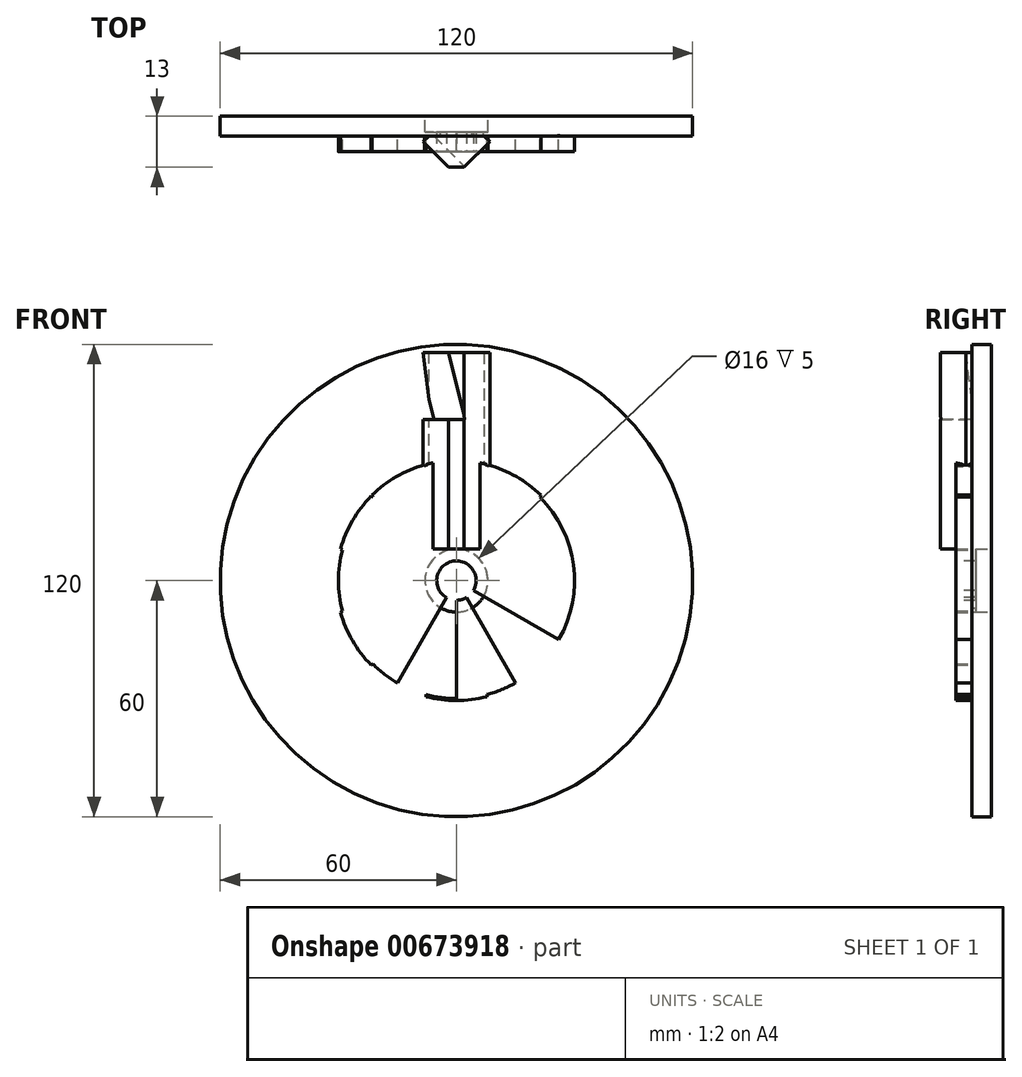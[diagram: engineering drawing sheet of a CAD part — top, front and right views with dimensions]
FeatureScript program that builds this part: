
annotation { "Feature Type Name" : "Feature", "Feature Type Description" : "" }
export const myFeature = defineFeature(function(context is Context, id is Id, definition is map)
    precondition{}
    {
        {
            var Q0;
            Q0=qCreatedBy(makeId("Front.planeOp"),FACE);
            var sketch = newSketch(context, id + "F0", { "sketchPlane" : qUnion([Q0])});
            skCircle(sketch, "E0", {"center": v(0, 0) * mm, "radius": 60 * mm});
            skCircle(sketch, "E1", {"center": v(0, 0) * mm, "radius": 30 * mm});
            skLineSegment(sketch, "E2", {"start": v(0, 60) * mm, "end": v(0, -60) * mm});
            skLineSegment(sketch, "E3", {"start": v(-60, 0) * mm, "end": v(60, 0) * mm});
            skLineSegment(sketch, "E4", {"start": v(0, 0) * mm, "end": v(51.96, -30) * mm});
            skLineSegment(sketch, "E5", {"start": v(51.96, -30) * mm, "end": v(-51.96, 30) * mm});
            skLineSegment(sketch, "E6", {"start": v(0, 0) * mm, "end": v(30, -51.96) * mm});
            skLineSegment(sketch, "E7", {"start": v(30, -51.96) * mm, "end": v(-30, 51.96) * mm});
            skLineSegment(sketch, "E8", {"start": v(0, 0) * mm, "end": v(-30, -51.96) * mm});
            skLineSegment(sketch, "E9", {"start": v(-30, -51.96) * mm, "end": v(30, 51.96) * mm});
            skLineSegment(sketch, "E10", {"start": v(0, 0) * mm, "end": v(51.96, 30) * mm});
            skLineSegment(sketch, "E11", {"start": v(51.96, 30) * mm, "end": v(-51.96, -30) * mm});
            skCircle(sketch, "E12", {"center": v(0, 0) * mm, "radius": 57.5 * mm});
            skLineSegment(sketch, "E13", {"start": v(0, 57.5) * mm, "end": v(-5, 57.28) * mm});
            skLineSegment(sketch, "E14", {"start": v(-28.75, 49.8) * mm, "end": v(-24.32, 52.1) * mm});
            skLineSegment(sketch, "E15", {"start": v(-24.32, 52.1) * mm, "end": v(-7.76, 28.98) * mm});
            skLineSegment(sketch, "E16", {"start": v(-7.76, 28.98) * mm, "end": v(-5, 57.28) * mm});
            skLineSegment(sketch, "E17.1.0", {"start": v(5, 57.28) * mm, "end": v(7.76, 28.98) * mm});
            skLineSegment(sketch, "E17.1.1", {"start": v(7.76, 28.98) * mm, "end": v(24.32, 52.1) * mm});
            skLineSegment(sketch, "E17.2.0", {"start": v(32.97, 47.11) * mm, "end": v(21.21, 21.21) * mm});
            skLineSegment(sketch, "E17.2.1", {"start": v(21.21, 21.21) * mm, "end": v(47.11, 32.97) * mm});
            skLineSegment(sketch, "E17.3.0", {"start": v(52.1, 24.32) * mm, "end": v(28.98, 7.76) * mm});
            skLineSegment(sketch, "E17.3.1", {"start": v(28.98, 7.76) * mm, "end": v(57.28, 5) * mm});
            skLineSegment(sketch, "E17.4.0", {"start": v(57.28, -5) * mm, "end": v(28.98, -7.76) * mm});
            skLineSegment(sketch, "E17.4.1", {"start": v(28.98, -7.76) * mm, "end": v(52.1, -24.32) * mm});
            skLineSegment(sketch, "E17.5.0", {"start": v(47.11, -32.97) * mm, "end": v(21.21, -21.21) * mm});
            skLineSegment(sketch, "E17.5.1", {"start": v(21.21, -21.21) * mm, "end": v(32.97, -47.11) * mm});
            skLineSegment(sketch, "E17.6.0", {"start": v(24.32, -52.1) * mm, "end": v(7.76, -28.98) * mm});
            skLineSegment(sketch, "E17.6.1", {"start": v(7.76, -28.98) * mm, "end": v(5, -57.28) * mm});
            skLineSegment(sketch, "E17.7.0", {"start": v(-5, -57.28) * mm, "end": v(-7.76, -28.98) * mm});
            skLineSegment(sketch, "E17.7.1", {"start": v(-7.76, -28.98) * mm, "end": v(-24.32, -52.1) * mm});
            skLineSegment(sketch, "E17.8.0", {"start": v(-32.97, -47.11) * mm, "end": v(-21.21, -21.21) * mm});
            skLineSegment(sketch, "E17.8.1", {"start": v(-21.21, -21.21) * mm, "end": v(-47.11, -32.97) * mm});
            skLineSegment(sketch, "E17.9.0", {"start": v(-52.1, -24.32) * mm, "end": v(-28.98, -7.76) * mm});
            skLineSegment(sketch, "E17.9.1", {"start": v(-28.98, -7.76) * mm, "end": v(-57.28, -5) * mm});
            skLineSegment(sketch, "E17.10.0", {"start": v(-57.28, 5) * mm, "end": v(-28.98, 7.76) * mm});
            skLineSegment(sketch, "E17.10.1", {"start": v(-28.98, 7.76) * mm, "end": v(-52.1, 24.32) * mm});
            skLineSegment(sketch, "E17.anchor1", {"start": v(0, 0) * mm, "end": v(-7.76, 28.98) * mm, "construction": true});
            skLineSegment(sketch, "E17.anchor2", {"start": v(0, 0) * mm, "end": v(-21.21, 21.21) * mm, "construction": true});
            skLineSegment(sketch, "E18.2.11.0", {"start": v(-47.11, 32.97) * mm, "end": v(-21.21, 21.21) * mm});
            skLineSegment(sketch, "E18.3.11.0", {"start": v(-21.21, 21.21) * mm, "end": v(-32.97, 47.11) * mm});
            skCircle(sketch, "E19", {"center": v(0, 0) * mm, "radius": 30.5 * mm});
            skSolve(sketch);
        }
        {
            var Q0;
            {var subQ1=sQuery(id+"F0.wireOp",EDGE,"E1");var subQ3=sQuery(id+"F0.wireOp",EDGE,"E2");var subQ4=makeQuery(id+"F0.imprint","INTERSECT",VERTEX,{"disambiguationData":[OD(0.0)],"derivedFrom":[subQ1,subQ3]});Q0=makeQuery(id+"F0.imprint","IMPRINT",FACE,{"disambiguationData":[TD([[makeQuery(id+"F0.imprint","IMPRINT",EDGE,{"disambiguationData":[TD([[subQ4,1.0]])],"derivedFrom":subQ3}),1.0]])]});}
            var Q1;
            {var subQ1=sQuery(id+"F0.wireOp",EDGE,"E1");var subQ3=sQuery(id+"F0.wireOp",EDGE,"E7");var subQ4=makeQuery(id+"F0.imprint","INTERSECT",VERTEX,{"disambiguationData":[OD(0.0)],"derivedFrom":[subQ1,subQ3]});Q1=makeQuery(id+"F0.imprint","IMPRINT",FACE,{"disambiguationData":[TD([[makeQuery(id+"F0.imprint","IMPRINT",EDGE,{"disambiguationData":[TD([[subQ4,-1.0]])],"derivedFrom":subQ3}),1.0]])]});}
            var Q2;
            {var subQ1=sQuery(id+"F0.wireOp",EDGE,"E1");var subQ3=sQuery(id+"F0.wireOp",EDGE,"E5");var subQ4=makeQuery(id+"F0.imprint","INTERSECT",VERTEX,{"disambiguationData":[OD(0.0)],"derivedFrom":[subQ1,subQ3]});Q2=makeQuery(id+"F0.imprint","IMPRINT",FACE,{"disambiguationData":[TD([[makeQuery(id+"F0.imprint","IMPRINT",EDGE,{"disambiguationData":[TD([[subQ4,-1.0]])],"derivedFrom":subQ3}),-1.0]])]});}
            var Q3;
            {var subQ1=sQuery(id+"F0.wireOp",EDGE,"E1");var subQ3=sQuery(id+"F0.wireOp",EDGE,"E5");var subQ4=makeQuery(id+"F0.imprint","INTERSECT",VERTEX,{"disambiguationData":[OD(0.0)],"derivedFrom":[subQ1,subQ3]});Q3=makeQuery(id+"F0.imprint","IMPRINT",FACE,{"disambiguationData":[TD([[makeQuery(id+"F0.imprint","IMPRINT",EDGE,{"disambiguationData":[TD([[subQ4,-1.0]])],"derivedFrom":subQ3}),1.0]])]});}
            var Q4;
            {var subQ1=sQuery(id+"F0.wireOp",EDGE,"E1");var subQ3=sQuery(id+"F0.wireOp",EDGE,"E3");var subQ4=makeQuery(id+"F0.imprint","INTERSECT",VERTEX,{"disambiguationData":[OD(1.0)],"derivedFrom":[subQ1,subQ3]});Q4=makeQuery(id+"F0.imprint","IMPRINT",FACE,{"disambiguationData":[TD([[makeQuery(id+"F0.imprint","IMPRINT",EDGE,{"disambiguationData":[TD([[subQ4,1.0]])],"derivedFrom":subQ3}),1.0]])]});}
            var Q5;
            {var subQ1=sQuery(id+"F0.wireOp",EDGE,"E1");var subQ3=sQuery(id+"F0.wireOp",EDGE,"E3");var subQ4=makeQuery(id+"F0.imprint","INTERSECT",VERTEX,{"disambiguationData":[OD(1.0)],"derivedFrom":[subQ1,subQ3]});Q5=makeQuery(id+"F0.imprint","IMPRINT",FACE,{"disambiguationData":[TD([[makeQuery(id+"F0.imprint","IMPRINT",EDGE,{"disambiguationData":[TD([[subQ4,1.0]])],"derivedFrom":subQ3}),-1.0]])]});}
            var Q6;
            {var subQ1=sQuery(id+"F0.wireOp",EDGE,"E1");var subQ3=sQuery(id+"F0.wireOp",EDGE,"E11");var subQ4=makeQuery(id+"F0.imprint","INTERSECT",VERTEX,{"disambiguationData":[OD(1.0)],"derivedFrom":[subQ1,subQ3]});Q6=makeQuery(id+"F0.imprint","IMPRINT",FACE,{"disambiguationData":[TD([[makeQuery(id+"F0.imprint","IMPRINT",EDGE,{"disambiguationData":[TD([[subQ4,-1.0]])],"derivedFrom":subQ3}),-1.0]])]});}
            var Q7;
            {var subQ1=sQuery(id+"F0.wireOp",EDGE,"E1");var subQ3=sQuery(id+"F0.wireOp",EDGE,"E11");var subQ4=makeQuery(id+"F0.imprint","INTERSECT",VERTEX,{"disambiguationData":[OD(1.0)],"derivedFrom":[subQ1,subQ3]});Q7=makeQuery(id+"F0.imprint","IMPRINT",FACE,{"disambiguationData":[TD([[makeQuery(id+"F0.imprint","IMPRINT",EDGE,{"disambiguationData":[TD([[subQ4,-1.0]])],"derivedFrom":subQ3}),1.0]])]});}
            var Q8;
            {var subQ1=sQuery(id+"F0.wireOp",EDGE,"E1");var subQ3=sQuery(id+"F0.wireOp",EDGE,"E9");var subQ4=makeQuery(id+"F0.imprint","INTERSECT",VERTEX,{"disambiguationData":[OD(1.0)],"derivedFrom":[subQ1,subQ3]});Q8=makeQuery(id+"F0.imprint","IMPRINT",FACE,{"disambiguationData":[TD([[makeQuery(id+"F0.imprint","IMPRINT",EDGE,{"disambiguationData":[TD([[subQ4,1.0]])],"derivedFrom":subQ3}),1.0]])]});}
            var Q9;
            {var subQ1=sQuery(id+"F0.wireOp",EDGE,"E1");var subQ3=sQuery(id+"F0.wireOp",EDGE,"E9");var subQ4=makeQuery(id+"F0.imprint","INTERSECT",VERTEX,{"disambiguationData":[OD(1.0)],"derivedFrom":[subQ1,subQ3]});Q9=makeQuery(id+"F0.imprint","IMPRINT",FACE,{"disambiguationData":[TD([[makeQuery(id+"F0.imprint","IMPRINT",EDGE,{"disambiguationData":[TD([[subQ4,1.0]])],"derivedFrom":subQ3}),-1.0]])]});}
            var Q10;
            {var subQ1=sQuery(id+"F0.wireOp",EDGE,"E1");var subQ3=sQuery(id+"F0.wireOp",EDGE,"E2");var subQ4=makeQuery(id+"F0.imprint","INTERSECT",VERTEX,{"disambiguationData":[OD(1.0)],"derivedFrom":[subQ1,subQ3]});Q10=makeQuery(id+"F0.imprint","IMPRINT",FACE,{"disambiguationData":[TD([[makeQuery(id+"F0.imprint","IMPRINT",EDGE,{"disambiguationData":[TD([[subQ4,-1.0]])],"derivedFrom":subQ3}),-1.0]])]});}
            var Q11;
            {var subQ1=sQuery(id+"F0.wireOp",EDGE,"E1");var subQ3=sQuery(id+"F0.wireOp",EDGE,"E2");var subQ4=makeQuery(id+"F0.imprint","INTERSECT",VERTEX,{"disambiguationData":[OD(1.0)],"derivedFrom":[subQ1,subQ3]});Q11=makeQuery(id+"F0.imprint","IMPRINT",FACE,{"disambiguationData":[TD([[makeQuery(id+"F0.imprint","IMPRINT",EDGE,{"disambiguationData":[TD([[subQ4,-1.0]])],"derivedFrom":subQ3}),1.0]])]});}
            var Q12;
            {var subQ1=sQuery(id+"F0.wireOp",EDGE,"E1");var subQ3=sQuery(id+"F0.wireOp",EDGE,"E7");var subQ4=makeQuery(id+"F0.imprint","INTERSECT",VERTEX,{"disambiguationData":[OD(1.0)],"derivedFrom":[subQ1,subQ3]});Q12=makeQuery(id+"F0.imprint","IMPRINT",FACE,{"disambiguationData":[TD([[makeQuery(id+"F0.imprint","IMPRINT",EDGE,{"disambiguationData":[TD([[subQ4,1.0]])],"derivedFrom":subQ3}),1.0]])]});}
            var Q13;
            {var subQ1=sQuery(id+"F0.wireOp",EDGE,"E1");var subQ3=sQuery(id+"F0.wireOp",EDGE,"E5");var subQ4=makeQuery(id+"F0.imprint","INTERSECT",VERTEX,{"disambiguationData":[OD(1.0)],"derivedFrom":[subQ1,subQ3]});Q13=makeQuery(id+"F0.imprint","IMPRINT",FACE,{"disambiguationData":[TD([[makeQuery(id+"F0.imprint","IMPRINT",EDGE,{"disambiguationData":[TD([[subQ4,1.0]])],"derivedFrom":subQ3}),1.0]])]});}
            var Q14;
            {var subQ1=sQuery(id+"F0.wireOp",EDGE,"E1");var subQ3=sQuery(id+"F0.wireOp",EDGE,"E5");var subQ4=makeQuery(id+"F0.imprint","INTERSECT",VERTEX,{"disambiguationData":[OD(1.0)],"derivedFrom":[subQ1,subQ3]});Q14=makeQuery(id+"F0.imprint","IMPRINT",FACE,{"disambiguationData":[TD([[makeQuery(id+"F0.imprint","IMPRINT",EDGE,{"disambiguationData":[TD([[subQ4,1.0]])],"derivedFrom":subQ3}),-1.0]])]});}
            var Q15;
            {var subQ1=sQuery(id+"F0.wireOp",EDGE,"E1");var subQ3=sQuery(id+"F0.wireOp",EDGE,"E3");var subQ4=makeQuery(id+"F0.imprint","INTERSECT",VERTEX,{"disambiguationData":[OD(0.0)],"derivedFrom":[subQ1,subQ3]});Q15=makeQuery(id+"F0.imprint","IMPRINT",FACE,{"disambiguationData":[TD([[makeQuery(id+"F0.imprint","IMPRINT",EDGE,{"disambiguationData":[TD([[subQ4,-1.0]])],"derivedFrom":subQ3}),-1.0]])]});}
            var Q16;
            {var subQ1=sQuery(id+"F0.wireOp",EDGE,"E1");var subQ3=sQuery(id+"F0.wireOp",EDGE,"E3");var subQ4=makeQuery(id+"F0.imprint","INTERSECT",VERTEX,{"disambiguationData":[OD(0.0)],"derivedFrom":[subQ1,subQ3]});Q16=makeQuery(id+"F0.imprint","IMPRINT",FACE,{"disambiguationData":[TD([[makeQuery(id+"F0.imprint","IMPRINT",EDGE,{"disambiguationData":[TD([[subQ4,-1.0]])],"derivedFrom":subQ3}),1.0]])]});}
            var Q17;
            {var subQ1=sQuery(id+"F0.wireOp",EDGE,"E1");var subQ3=sQuery(id+"F0.wireOp",EDGE,"E11");var subQ4=makeQuery(id+"F0.imprint","INTERSECT",VERTEX,{"disambiguationData":[OD(0.0)],"derivedFrom":[subQ1,subQ3]});Q17=makeQuery(id+"F0.imprint","IMPRINT",FACE,{"disambiguationData":[TD([[makeQuery(id+"F0.imprint","IMPRINT",EDGE,{"disambiguationData":[TD([[subQ4,1.0]])],"derivedFrom":subQ3}),1.0]])]});}
            var Q18;
            {var subQ1=sQuery(id+"F0.wireOp",EDGE,"E1");var subQ3=sQuery(id+"F0.wireOp",EDGE,"E11");var subQ4=makeQuery(id+"F0.imprint","INTERSECT",VERTEX,{"disambiguationData":[OD(0.0)],"derivedFrom":[subQ1,subQ3]});Q18=makeQuery(id+"F0.imprint","IMPRINT",FACE,{"disambiguationData":[TD([[makeQuery(id+"F0.imprint","IMPRINT",EDGE,{"disambiguationData":[TD([[subQ4,1.0]])],"derivedFrom":subQ3}),-1.0]])]});}
            var Q19;
            {var subQ1=sQuery(id+"F0.wireOp",EDGE,"E1");var subQ3=sQuery(id+"F0.wireOp",EDGE,"E9");var subQ4=makeQuery(id+"F0.imprint","INTERSECT",VERTEX,{"disambiguationData":[OD(0.0)],"derivedFrom":[subQ1,subQ3]});Q19=makeQuery(id+"F0.imprint","IMPRINT",FACE,{"disambiguationData":[TD([[makeQuery(id+"F0.imprint","IMPRINT",EDGE,{"disambiguationData":[TD([[subQ4,-1.0]])],"derivedFrom":subQ3}),-1.0]])]});}
            var Q20;
            {var subQ1=sQuery(id+"F0.wireOp",EDGE,"E1");var subQ3=sQuery(id+"F0.wireOp",EDGE,"E9");var subQ4=makeQuery(id+"F0.imprint","INTERSECT",VERTEX,{"disambiguationData":[OD(0.0)],"derivedFrom":[subQ1,subQ3]});Q20=makeQuery(id+"F0.imprint","IMPRINT",FACE,{"disambiguationData":[TD([[makeQuery(id+"F0.imprint","IMPRINT",EDGE,{"disambiguationData":[TD([[subQ4,-1.0]])],"derivedFrom":subQ3}),1.0]])]});}
            var Q21;
            {var subQ1=sQuery(id+"F0.wireOp",EDGE,"E1");var subQ3=sQuery(id+"F0.wireOp",EDGE,"E7");var subQ4=makeQuery(id+"F0.imprint","INTERSECT",VERTEX,{"disambiguationData":[OD(1.0)],"derivedFrom":[subQ1,subQ3]});Q21=makeQuery(id+"F0.imprint","IMPRINT",FACE,{"disambiguationData":[TD([[makeQuery(id+"F0.imprint","IMPRINT",EDGE,{"disambiguationData":[TD([[subQ4,1.0]])],"derivedFrom":subQ3}),-1.0]])]});}
            var Q22;
            {var subQ0=sQuery(id+"F0.wireOp",EDGE,"E1");var subQ2=sQuery(id+"F0.wireOp",EDGE,"E7");var subQ3=makeQuery(id+"F0.imprint","INTERSECT",VERTEX,{"disambiguationData":[OD(1.0)],"derivedFrom":[subQ0,subQ2]});Q22=makeQuery(id+"F0.imprint","IMPRINT",FACE,{"disambiguationData":[TD([[makeQuery(id+"F0.imprint","IMPRINT",EDGE,{"disambiguationData":[TD([[subQ3,-1.0]])],"derivedFrom":subQ0}),1.0]])]});}
            var Q23;
            {var subQ0=sQuery(id+"F0.wireOp",EDGE,"E1");var subQ2=sQuery(id+"F0.wireOp",EDGE,"E5");var subQ3=makeQuery(id+"F0.imprint","INTERSECT",VERTEX,{"disambiguationData":[OD(1.0)],"derivedFrom":[subQ0,subQ2]});Q23=makeQuery(id+"F0.imprint","IMPRINT",FACE,{"disambiguationData":[TD([[makeQuery(id+"F0.imprint","IMPRINT",EDGE,{"disambiguationData":[TD([[subQ3,-1.0]])],"derivedFrom":subQ0}),1.0]])]});}
            var Q24;
            {var subQ0=sQuery(id+"F0.wireOp",EDGE,"E1");var subQ2=sQuery(id+"F0.wireOp",EDGE,"E3");var subQ3=makeQuery(id+"F0.imprint","INTERSECT",VERTEX,{"disambiguationData":[OD(0.0)],"derivedFrom":[subQ0,subQ2]});Q24=makeQuery(id+"F0.imprint","IMPRINT",FACE,{"disambiguationData":[TD([[makeQuery(id+"F0.imprint","IMPRINT",EDGE,{"disambiguationData":[TD([[subQ3,-1.0]])],"derivedFrom":subQ0}),1.0]])]});}
            var Q25;
            {var subQ0=sQuery(id+"F0.wireOp",EDGE,"E1");var subQ2=sQuery(id+"F0.wireOp",EDGE,"E9");var subQ3=makeQuery(id+"F0.imprint","INTERSECT",VERTEX,{"disambiguationData":[OD(0.0)],"derivedFrom":[subQ0,subQ2]});Q25=makeQuery(id+"F0.imprint","IMPRINT",FACE,{"disambiguationData":[TD([[makeQuery(id+"F0.imprint","IMPRINT",EDGE,{"disambiguationData":[TD([[subQ3,-1.0]])],"derivedFrom":subQ0}),1.0]])]});}
            var Q26;
            {var subQ0=sQuery(id+"F0.wireOp",EDGE,"E1");var subQ2=sQuery(id+"F0.wireOp",EDGE,"E2");var subQ3=makeQuery(id+"F0.imprint","INTERSECT",VERTEX,{"disambiguationData":[OD(0.0)],"derivedFrom":[subQ0,subQ2]});Q26=makeQuery(id+"F0.imprint","IMPRINT",FACE,{"disambiguationData":[TD([[makeQuery(id+"F0.imprint","IMPRINT",EDGE,{"disambiguationData":[TD([[subQ3,-1.0]])],"derivedFrom":subQ0}),1.0]])]});}
            var Q27;
            {var subQ0=sQuery(id+"F0.wireOp",EDGE,"E1");var subQ2=sQuery(id+"F0.wireOp",EDGE,"E7");var subQ3=makeQuery(id+"F0.imprint","INTERSECT",VERTEX,{"disambiguationData":[OD(0.0)],"derivedFrom":[subQ0,subQ2]});Q27=makeQuery(id+"F0.imprint","IMPRINT",FACE,{"disambiguationData":[TD([[makeQuery(id+"F0.imprint","IMPRINT",EDGE,{"disambiguationData":[TD([[subQ3,-1.0]])],"derivedFrom":subQ0}),1.0]])]});}
            var Q28;
            {var subQ0=sQuery(id+"F0.wireOp",EDGE,"E1");var subQ2=sQuery(id+"F0.wireOp",EDGE,"E11");var subQ3=makeQuery(id+"F0.imprint","INTERSECT",VERTEX,{"disambiguationData":[OD(0.0)],"derivedFrom":[subQ0,subQ2]});Q28=makeQuery(id+"F0.imprint","IMPRINT",FACE,{"disambiguationData":[TD([[makeQuery(id+"F0.imprint","IMPRINT",EDGE,{"disambiguationData":[TD([[subQ3,-1.0]])],"derivedFrom":subQ0}),1.0]])]});}
            var Q29;
            {var subQ0=sQuery(id+"F0.wireOp",EDGE,"E1");var subQ2=sQuery(id+"F0.wireOp",EDGE,"E3");var subQ3=makeQuery(id+"F0.imprint","INTERSECT",VERTEX,{"disambiguationData":[OD(1.0)],"derivedFrom":[subQ0,subQ2]});Q29=makeQuery(id+"F0.imprint","IMPRINT",FACE,{"disambiguationData":[TD([[makeQuery(id+"F0.imprint","IMPRINT",EDGE,{"disambiguationData":[TD([[subQ3,-1.0]])],"derivedFrom":subQ0}),1.0]])]});}
            var Q30;
            {var subQ0=sQuery(id+"F0.wireOp",EDGE,"E1");var subQ2=sQuery(id+"F0.wireOp",EDGE,"E5");var subQ3=makeQuery(id+"F0.imprint","INTERSECT",VERTEX,{"disambiguationData":[OD(0.0)],"derivedFrom":[subQ0,subQ2]});Q30=makeQuery(id+"F0.imprint","IMPRINT",FACE,{"disambiguationData":[TD([[makeQuery(id+"F0.imprint","IMPRINT",EDGE,{"disambiguationData":[TD([[subQ3,-1.0]])],"derivedFrom":subQ0}),1.0]])]});}
            var Q31;
            {var subQ0=sQuery(id+"F0.wireOp",EDGE,"E1");var subQ2=sQuery(id+"F0.wireOp",EDGE,"E11");var subQ3=makeQuery(id+"F0.imprint","INTERSECT",VERTEX,{"disambiguationData":[OD(1.0)],"derivedFrom":[subQ0,subQ2]});Q31=makeQuery(id+"F0.imprint","IMPRINT",FACE,{"disambiguationData":[TD([[makeQuery(id+"F0.imprint","IMPRINT",EDGE,{"disambiguationData":[TD([[subQ3,-1.0]])],"derivedFrom":subQ0}),1.0]])]});}
            var Q32;
            {var subQ0=sQuery(id+"F0.wireOp",EDGE,"E1");var subQ2=sQuery(id+"F0.wireOp",EDGE,"E9");var subQ3=makeQuery(id+"F0.imprint","INTERSECT",VERTEX,{"disambiguationData":[OD(1.0)],"derivedFrom":[subQ0,subQ2]});Q32=makeQuery(id+"F0.imprint","IMPRINT",FACE,{"disambiguationData":[TD([[makeQuery(id+"F0.imprint","IMPRINT",EDGE,{"disambiguationData":[TD([[subQ3,-1.0]])],"derivedFrom":subQ0}),1.0]])]});}
            var Q33;
            {var subQ0=sQuery(id+"F0.wireOp",EDGE,"E1");var subQ2=sQuery(id+"F0.wireOp",EDGE,"E2");var subQ3=makeQuery(id+"F0.imprint","INTERSECT",VERTEX,{"disambiguationData":[OD(1.0)],"derivedFrom":[subQ0,subQ2]});Q33=makeQuery(id+"F0.imprint","IMPRINT",FACE,{"disambiguationData":[TD([[makeQuery(id+"F0.imprint","IMPRINT",EDGE,{"disambiguationData":[TD([[subQ3,-1.0]])],"derivedFrom":subQ0}),1.0]])]});}
            var Q34;
            {var subQ1=sQuery(id+"F0.wireOp",EDGE,"E1");var subQ3=sQuery(id+"F0.wireOp",EDGE,"E7");var subQ4=makeQuery(id+"F0.imprint","INTERSECT",VERTEX,{"disambiguationData":[OD(0.0)],"derivedFrom":[subQ1,subQ3]});Q34=makeQuery(id+"F0.imprint","IMPRINT",FACE,{"disambiguationData":[TD([[makeQuery(id+"F0.imprint","IMPRINT",EDGE,{"disambiguationData":[TD([[subQ4,-1.0]])],"derivedFrom":subQ3}),-1.0]])]});}
            var Q35;
            {var subQ1=sQuery(id+"F0.wireOp",EDGE,"E1");var subQ3=sQuery(id+"F0.wireOp",EDGE,"E2");var subQ4=makeQuery(id+"F0.imprint","INTERSECT",VERTEX,{"disambiguationData":[OD(0.0)],"derivedFrom":[subQ1,subQ3]});Q35=makeQuery(id+"F0.imprint","IMPRINT",FACE,{"disambiguationData":[TD([[makeQuery(id+"F0.imprint","IMPRINT",EDGE,{"disambiguationData":[TD([[subQ4,1.0]])],"derivedFrom":subQ3}),-1.0]])]});}
            extrude(context, id + "F1", {"entities" : qUnion([Q0, Q1, Q2, Q3, Q4, Q5, Q6, Q7, Q8, Q9, Q10, Q11, Q12, Q13, Q14, Q15, Q16, Q17, Q18, Q19, Q20, Q21, Q22, Q23, Q24, Q25, Q26, Q27, Q28, Q29, Q30, Q31, Q32, Q33, Q34, Q35]), "endBound" : BoundingType.SYMMETRIC, "depth" : 5 * mm, "offsetDistance" : 25 * mm});
        }
        {
            var Q0;
            Q0=qCreatedBy(makeId("Top.planeOp"),FACE);
            var sketch = newSketch(context, id + "F2", { "sketchPlane" : qUnion([Q0])});
            skCircle(sketch, "E20", {"center": v(0, 0) * mm, "radius": 25 * mm});
            skLineSegment(sketch, "E21", {"start": v(0, 0) * mm, "end": v(0, 5) * mm});
            skLineSegment(sketch, "E22", {"start": v(0, 5) * mm, "end": v(0, -5) * mm});
            skSolve(sketch);
        }
        {
            var Q0;
            Q0=sQuery(id+"F2.wireOp",EDGE,"E20");
            cPlane(context, id + "F3", {"entities" : qUnion([Q0]), "cplaneType" : CPlaneType.LINE_ANGLE, "offset" : 25 * mm, "angle" : 45 * degree, "width" : 150 * mm, "height" : 150 * mm});
        }
        {
            var Q0;
            Q0=qCreatedBy(id+"F3.planeOp",FACE);
            var sketch = newSketch(context, id + "F4", { "sketchPlane" : qUnion([Q0])});
            skLineSegment(sketch, "E23", {"start": v(0, 0) * mm, "end": v(0, 58) * mm});
            skLineSegment(sketch, "E24", {"start": v(0, 58) * mm, "end": v(-6, 58) * mm});
            skLineSegment(sketch, "E25.bottom", {"start": v(-6, 58) * mm, "end": v(6, 58) * mm});
            skLineSegment(sketch, "E25.top", {"start": v(-6, 8) * mm, "end": v(6, 8) * mm});
            skLineSegment(sketch, "E25.left", {"start": v(-6, 58) * mm, "end": v(-6, 8) * mm});
            skLineSegment(sketch, "E25.right", {"start": v(6, 58) * mm, "end": v(6, 8) * mm});
            skSolve(sketch);
        }
        {
            var Q0;
            Q0 = qSketchRegion(id + "F4", true);
            extrude(context, id + "F5", {"entities" : qUnion([Q0]), "operationType" : NewBodyOperationType.ADD, "endBound" : BoundingType.SYMMETRIC, "depth" : 12 * mm, "offsetDistance" : 25 * mm});
        }
        {
            var Q0;
            Q0=qCreatedBy(makeId("Front.planeOp"),FACE);
            var sketch = newSketch(context, id + "F6", { "sketchPlane" : qUnion([Q0])});
            skCircle(sketch, "E26", {"center": v(0, 0) * mm, "radius": 5 * mm});
            skSolve(sketch);
        }
        {
            var Q0;
            Q0 = qSketchRegion(id + "F6", true);
            extrude(context, id + "F7", {"entities" : qUnion([Q0]), "operationType" : NewBodyOperationType.REMOVE, "endBound" : BoundingType.SYMMETRIC, "oppositeDirection" : true, "depth" : 25 * mm, "offsetDistance" : 25 * mm});
        }
        {
            var Q0;
            Q0=makeQuery(id+"F5.opExtrude","SWEPT_FACE",FACE,{"disambiguationData":[OSD([sQuery(id+"F4.wireOp",EDGE,"E25.left")])]});
            var sketch = newSketch(context, id + "F8", { "sketchPlane" : qUnion([Q0])});
            skLineSegment(sketch, "E27", {"start": v(-6, 58) * mm, "end": v(0, 58) * mm});
            skLineSegment(sketch, "E28", {"start": v(-6, 58) * mm, "end": v(0, 23.97) * mm});
            skLineSegment(sketch, "E29", {"start": v(0, 58) * mm, "end": v(0, 23.97) * mm});
            skLineSegment(sketch, "E30", {"start": v(0, 23.97) * mm, "end": v(-8.33, 23.97) * mm});
            skLineSegment(sketch, "E31", {"start": v(-8.33, 23.97) * mm, "end": v(-8.33, 58) * mm});
            skLineSegment(sketch, "E32", {"start": v(-8.33, 58) * mm, "end": v(-6, 58) * mm});
            skLineSegment(sketch, "E33", {"start": v(-8.33, 23.97) * mm, "end": v(-6.83, 23.97) * mm});
            skLineSegment(sketch, "E34", {"start": v(-8.33, 40.99) * mm, "end": v(0, 40.99) * mm});
            skSolve(sketch);
        }
        {
            var Q0;
            {var subQ0=sQuery(id+"F8.wireOp",EDGE,"E28");Q0=makeQuery(id+"F8.imprint","IMPRINT",FACE,{"disambiguationData":[TD([[makeQuery(id+"F8.imprint","IMPRINT",EDGE,{"derivedFrom":subQ0}),-1.0]])]});}
            var Q1;
            {var subQ0=sQuery(id+"F8.wireOp",EDGE,"E32");Q1=makeQuery(id+"F8.imprint","IMPRINT",FACE,{"disambiguationData":[TD([[makeQuery(id+"F8.imprint","IMPRINT",EDGE,{"derivedFrom":subQ0}),-1.0]])]});}
            extrude(context, id + "F9", {"entities" : qUnion([Q0, Q1]), "operationType" : NewBodyOperationType.REMOVE, "oppositeDirection" : true, "depth" : 25 * mm, "offsetDistance" : 25 * mm});
        }
        {
            var Q0;
            Q0=makeQuery(id+"F9.boolean.opBoolean","COPY",FACE,{"derivedFrom":makeQuery(id+"F9.opExtrude","SWEPT_FACE",FACE,{"disambiguationData":[OSD([sQuery(id+"F8.wireOp",EDGE,"E28")])]})});
            var sketch = newSketch(context, id + "F10", { "sketchPlane" : qUnion([Q0])});
            skLineSegment(sketch, "E35", {"start": v(9.95, 57.3) * mm, "end": v(9.27, 53.36) * mm});
            skCircle(sketch, "E36", {"center": v(9.27, 53.36) * mm, "radius": 1.5 * mm});
            skSolve(sketch);
        }
        {
            var Q0;
            Q0=qCreatedBy(makeId("Right.planeOp"),FACE);
            var sketch = newSketch(context, id + "F11", { "sketchPlane" : qUnion([Q0])});
            skLineSegment(sketch, "E37.bottom", {"start": v(6.5, -65) * mm, "end": v(-6.5, -65) * mm});
            skLineSegment(sketch, "E37.top", {"start": v(6.5, 65) * mm, "end": v(-6.5, 65) * mm});
            skLineSegment(sketch, "E37.left", {"start": v(6.5, -65) * mm, "end": v(6.5, 65) * mm});
            skLineSegment(sketch, "E37.right", {"start": v(-6.5, -65) * mm, "end": v(-6.5, 65) * mm});
            skPoint(sketch, "E37.middle", {"position": v(0, 0) * mm});
            skLineSegment(sketch, "E38.bottom", {"start": v(40.87, -77.07) * mm, "end": v(-40.87, -77.07) * mm});
            skLineSegment(sketch, "E38.top", {"start": v(40.87, 77.07) * mm, "end": v(-40.87, 77.07) * mm});
            skLineSegment(sketch, "E38.left", {"start": v(40.87, -77.07) * mm, "end": v(40.87, 77.07) * mm});
            skLineSegment(sketch, "E38.right", {"start": v(-40.87, -77.07) * mm, "end": v(-40.87, 77.07) * mm});
            skSolve(sketch);
        }
        {
            var Q0;
            Q0 = qSketchRegion(id + "F11", true);
            extrude(context, id + "F12", {"entities" : qUnion([Q0]), "operationType" : NewBodyOperationType.REMOVE, "endBound" : BoundingType.SYMMETRIC, "oppositeDirection" : true, "depth" : 143.4 * mm, "offsetDistance" : 25 * mm});
        }
        {
            var Q0;
            Q0=qCreatedBy(makeId("Front.planeOp"),FACE);
            cPlane(context, id + "F13", {"entities" : qUnion([Q0]), "cplaneType" : CPlaneType.OFFSET, "offset" : 6.5 * mm, "oppositeDirection" : true, "width" : 150 * mm, "height" : 150 * mm});
        }
        {
            var Q0;
            Q0=qCreatedBy(id+"F13.planeOp",FACE);
            var sketch = newSketch(context, id + "F14", { "sketchPlane" : qUnion([Q0])});
            skCircle(sketch, "E39", {"center": v(0, 0) * mm, "radius": 8 * mm});
            skCircle(sketch, "E40", {"center": v(0, 0) * mm, "radius": 60 * mm});
            skCircle(sketch, "E41", {"center": v(0, 0) * mm, "radius": 74.52 * mm});
            skSolve(sketch);
        }
        {
            var Q0;
            Q0=makeQuery(id+"F14.imprint","IMPRINT",FACE,{"disambiguationData":[TD([[makeQuery(id+"F14.imprint","IMPRINT",EDGE,{"derivedFrom":sQuery(id+"F14.wireOp",EDGE,"E39")}),-1.0]])]});
            extrude(context, id + "F15", {"entities" : qUnion([Q0]), "operationType" : NewBodyOperationType.ADD, "depth" : 5 * mm, "offsetDistance" : 25 * mm});
        }
        {
            var Q0;
            Q0=makeQuery(id+"F10.imprint","IMPRINT",FACE,{"disambiguationData":[TD([[makeQuery(id+"F10.imprint","IMPRINT",EDGE,{"derivedFrom":sQuery(id+"F10.wireOp",EDGE,"E36")}),1.0]])]});
            extrude(context, id + "F16", {"entities" : qUnion([Q0]), "operationType" : NewBodyOperationType.REMOVE, "oppositeDirection" : true, "depth" : 25 * mm, "offsetDistance" : 25 * mm});
        }
        {
            var Q0;
            Q0=makeQuery(id+"F14.imprint","IMPRINT",FACE,{"disambiguationData":[TD([[makeQuery(id+"F14.imprint","IMPRINT",EDGE,{"derivedFrom":sQuery(id+"F14.wireOp",EDGE,"E40")}),-1.0]])]});
            extrude(context, id + "F17", {"entities" : qUnion([Q0]), "operationType" : NewBodyOperationType.REMOVE, "endBound" : BoundingType.SYMMETRIC, "oppositeDirection" : true, "depth" : 25 * mm, "offsetDistance" : 25 * mm});
        }
    });
